# Revit family: FP_Revit_18_OS30NPX1_Steam_Oven_90001973A
name_source: partatom
category: Specialty Equipment
revit_build: Autodesk Revit 2018 (Build: 20170223_1515(x64)
units: mm (PartAtom-declared; Revit-internal decimal feet)

## family parameters
Always vertical = Yes
Cut with Voids When Loaded = Yes
OmniClass Number = 23.40.40.14.17.11
OmniClass Title = Cookers, Ovens, Stoves
Part Type = Normal
Room Calculation Point = No
Round Connector Dimension = Use Diameter
Shared = No
Work Plane-Based = No

## types (2) — shared parameters
Cavity - Depth = 560 mm  [stored 1.83727 ft]
Cavity - Height = 474 mm  [stored 1.55512 ft]
Cavity - Width = 762 mm  [stored 2.5 ft]
Chassis - Depth = 528 mm  [stored 1.73228 ft]
Chassis - Height = 447 mm
Chassis - Width = 645 mm  [stored 2.11614 ft]
Connector Description - Electrical = 120/208 V - 120/240 V, 60 Hz, 15 A circuit
Manufacturer = Fisher & Paykel Appliances
Material - Body = Fisher & Paykel - Grey
Material - Display Panel = Fisher & Paykel - Black
Material - Front = Fisher & Paykel - Stainless Steel
Material - Glass = Fisher & Paykel - Glass, Black
Material - Handle = Fisher & Paykel - Stainless Steel
Material - Logo = Fisher & Paykel - Steel, Chrome Plated
Material - Structure = Fisher & Paykel - Black
Material - Trim = Fisher & Paykel - Steel, Chrome Plated
Product - Depth = 623 mm  [stored 2.04396 ft]
Product - Height = 470 mm  [stored 1.54199 ft]
Product - Width = 758 mm  [stored 2.48688 ft]
URL = www.fisherpaykel.com
Visibility - Clearance Required = Yes

## per-type parameters (varying)
| type | Description |
| OS30NPX1 | 30" Combination Steam Oven |
| OM30NPX1 | 30" Convection Speed Oven |

note: column(s) folded — value = type name in every type: Model

note: [stored X ft] marks values corroborated as IEEE doubles in the binary element streams (Revit-internal decimal feet)

## geometry (parser evidence)
native form markers: Sweep x2
no freeform markers — native parametric forms only
